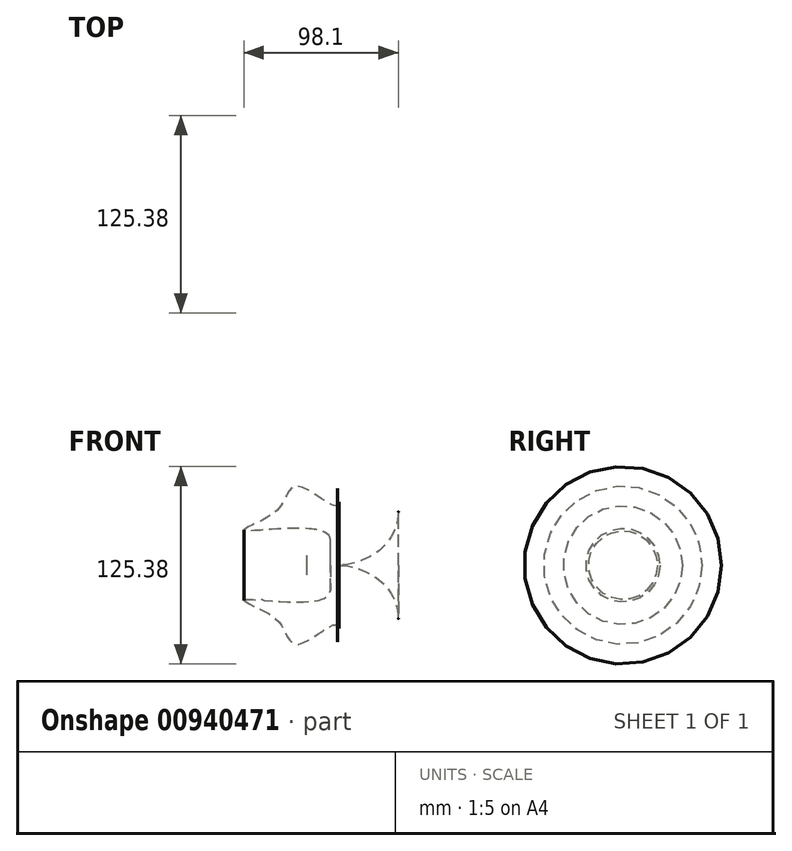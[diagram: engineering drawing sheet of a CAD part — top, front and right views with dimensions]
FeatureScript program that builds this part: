
annotation { "Feature Type Name" : "Feature", "Feature Type Description" : "" }
export const myFeature = defineFeature(function(context is Context, id is Id, definition is map)
    precondition{}
    {
        {
            var Q0;
            Q0=qCreatedBy(makeId("Top.planeOp"),FACE);
            var sketch = newSketch(context, id + "F0", { "sketchPlane" : qUnion([Q0])});
            skFitSpline(sketch, "E0", {"points": [v(-41.03, 40.01) * mm, v(-30.85, 51.97) * mm, v(-23.59, 59.26) * mm, v(-1.36, 47.37) * mm, v(2.78, 47.63) * mm, v(2.26, 56.8) * mm, v(8.6, 70.9) * mm, v(36, 58.62) * mm, v(34.7, 24.62) * mm, v(-1.87, 8.98) * mm, v(-17.24, 15.46) * mm, v(-4.07, 21.33) * mm, v(-6.79, 30.31) * mm, v(-57.19, 31.1) * mm, v(-41.03, 40.01) * mm]});
            skLineSegment(sketch, "E1", {"start": v(-31.74, 8.97) * mm, "end": v(68.76, 8.97) * mm});
            skSolve(sketch);
        }
        {
            var Q0;
            {var subQ0=sQuery(id+"F0.wireOp",EDGE,"e4973a42-3143-47b0-8c88-945c9709de0b0.MirrorC");var subQ1=sQuery(id+"F0.wireOp",EDGE,"E0");var subQ2=makeQuery(id+"F0.imprint","INTERSECT",VERTEX,{"disambiguationData":[OD(0.0)],"derivedFrom":[subQ1,subQ0]});Q0=makeQuery(id+"F0.imprint","IMPRINT",FACE,{"disambiguationData":[TD([[makeQuery(id+"F0.imprint","IMPRINT",EDGE,{"disambiguationData":[TD([[subQ2,-1.0]])],"derivedFrom":subQ1}),-1.0]])]});}
            var Q1;
            Q1=sQuery(id+"F0.wireOp",EDGE,"E1");
            revolve(context, id + "F1", {"surfaceOperationType" : NewSurfaceOperationType.NEW, "entities" : qUnion([Q0]), "axis" : qUnion([Q1]), "revolveType" : RevolveType.FULL, "oppositeDirection" : true});
        }
        {
            var Q0;
            Q0=makeQuery(id+"F1.opRevolve","SWEPT_BODY",BODY,{"disambiguationData":[OSD([sQuery(id+"F0.wireOp",EDGE,"E0"),sQuery(id+"F0.wireOp",EDGE,"E1")])]});
            var Q1;
            Q1=qCreatedBy(makeId("Top.planeOp"),FACE);
            transform(context, id + "F2", {"entities" : qUnion([Q0]), "transformType" : TransformType.TRANSLATION_DISTANCE, "transformDirection" : qUnion([Q1]), "distance" : 50 * mm, "makeCopy" : false});
        }
    });
